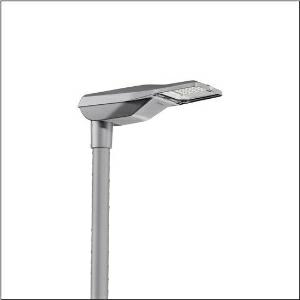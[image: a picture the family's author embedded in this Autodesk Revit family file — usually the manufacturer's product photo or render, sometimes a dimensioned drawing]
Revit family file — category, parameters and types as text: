
# Revit family: streetlight_sl_21_iq_micro___stw1_0a_5xe1e41g08db_19ca
name_source: partatom
category: Lighting Fixtures
units: mm (PartAtom-declared; Revit-internal decimal feet)

## family parameters
Cut with Voids When Loaded = No
Host = Face
Light Source = No
Part Type = Normal
Room Calculation Point = No
Round Connector Dimension = Use Diameter
Shared = No

## types (1)
- --- (1 x LED, 5010 lm, 36.4 W, 4000K)
    Apparent Load = 36 VA
    CIE Flux Codes = 38 75 98 100 100
    Color Rendering = 70
    Color Temperature = 4000K
    Default Elevation = 1800 mm
    Description = Streetlight SL 21 iQ micro, mast luminaire, primary light control with lens, of PMMA, primary optical cover: cover, of toughened safety glass, transparent, light distribution: STW1.0a, light emission: direct distribution, primary light characteristic: asymmetric, installation type: post-top, side-entry, LED, High Power LED, rated luminous flux: 5.010lm, luminous efficacy: 138lm/W, light colour: 740, colour temperature: 4000K, control gear: iQ Street-Remote, control: Street-Remote, Auto-Match, Temp-Guard, Lumen-Switch, Night-Set, Smart-Wire, Light-Fading, Desk-Remote (wireless, voltage-free reading and setting of iQ features in the workshop via application-optimized NFC function/RFID function), optimised constant luminous flux control (CLO 2.0), pre-setting: linear dimming characteristic, mains connection: 220..240V, AC, 50/60Hz, start of lifetime: 36W, end of service life: 38W, reduction: 16W, luminaire housing, of diecast aluminium, powder-coated, Siteco® metallic grey (DB 702S), corrosivity category C5 mid according to DIN EN ISO 12944, please order mast flange separately, inclination adjustable: 0°, 5°, 10°, 15°, sealing non-destructively replaceable, multi-level sealing system, length: 528mm, width: 235mm, height: 110mm, mast flange for spigot size: 42mm (side-entry): 5XC10008XM4, 60/48mm (side-entry/post-top): 5XC10108XM2, 76/60mm (side-entry/post-top): 5XC10108XM1, protection rating (complete): IP66, insulation class (complete): insulation class II (safety insulation), certification: CE, ENEC, ENEC+, VDE, impact resistance: IK10, permissible operating ambient temperature for outdoor applications: -40..+50°C, standard-compliant lighting for roads and squares, packaging unit: 1 piece

Light Distribution: STW1.0a
    Height = 110 mm
    Lamp = 1 x LED
    Lamp Light Flux = 5010 lm
    Lamp Power = 36.4 W
    Lamp count = 1
    Length = 528 mm
    Luminous efficacy = 138 lm/W
    Manufacturer = Siteco
    ModVariant = No
    Model = 5XE1E41G08DB
    Number of Poles = 1
    OnlyDefault = Yes
    Power Factor = 1
    Product Name = Streetlight SL 21 iQ micro | STW1.0a
    Product group = mast luminaire | pylon top
    ProductGroupID = 6100
    Protection Class = Protection class II
    Protection Degree = IP 66
    RLX_Detail_Level = 1
    RLX_Emergency_Light_Flux = 0 lm
    RLX_Emergency_Type = 0
    RLX_Emergency_Type_DB = No
    RlxData = <blob elided: 99217 chars, md5=8d5f8520>
    Socket = socket
    Standby Power = 0 W
    System Light Flux = 5010 lm
    System Power = 36 W
    Type Comments = factory setting: luminous flux: 100 % | dim-lin: 254 | 715 mA
    Type Image = l_1006881.jpg
    URL = http://relux.com
    VarID = @adj_176865
    Voltage = 0 V
    Weight = 0.00 kg
    Width = 235 mm

## geometry (parser evidence)
native form markers: Blend x4, Sweep x10
no freeform markers — native parametric forms only
